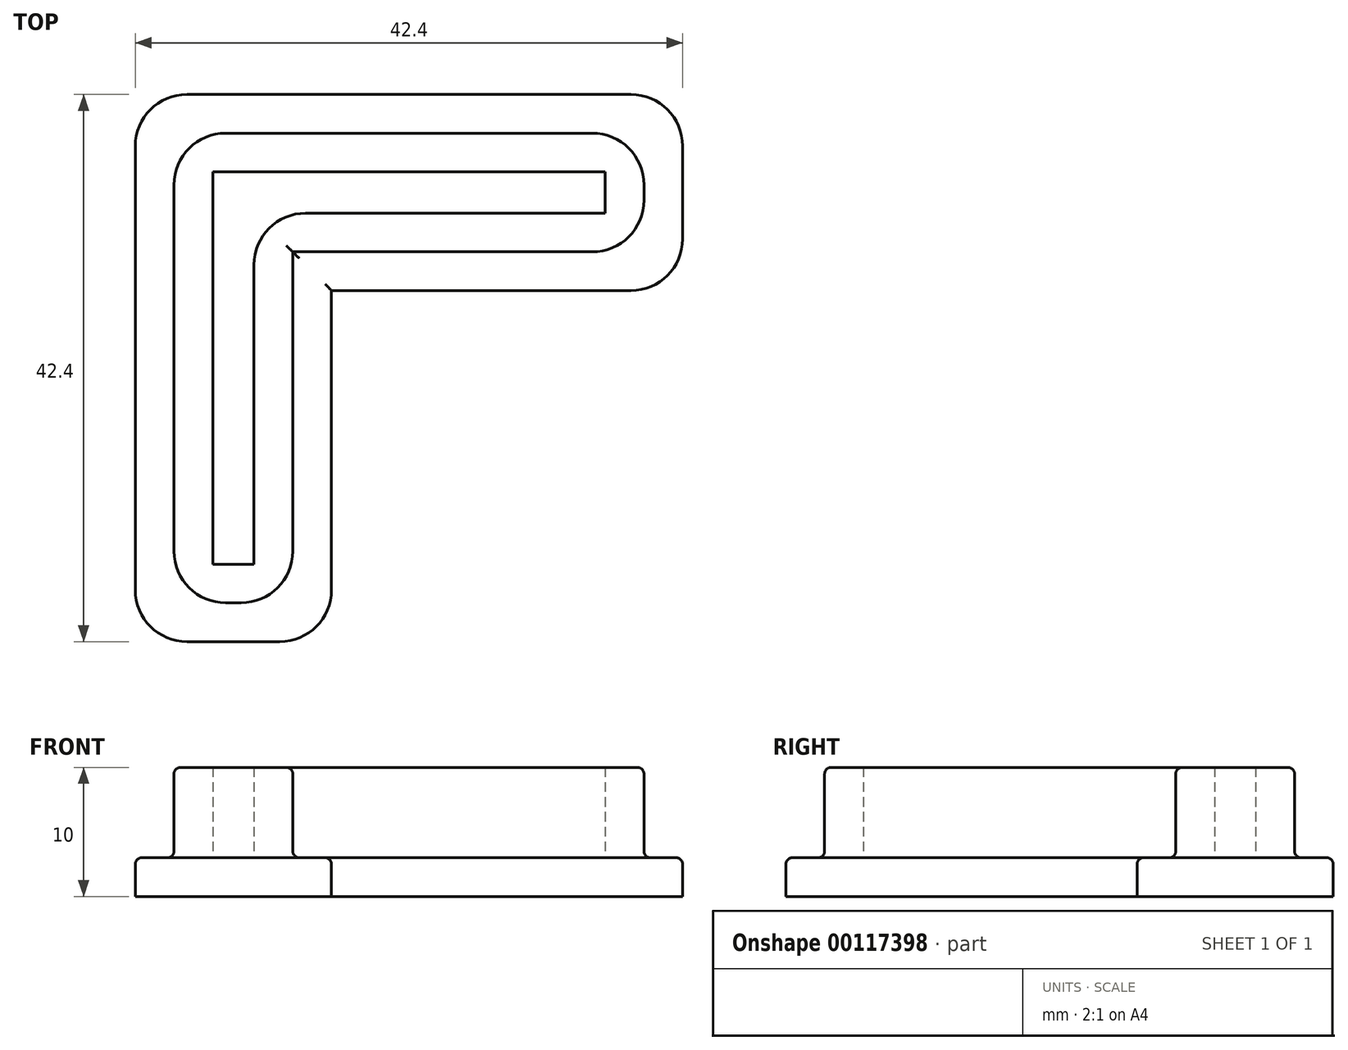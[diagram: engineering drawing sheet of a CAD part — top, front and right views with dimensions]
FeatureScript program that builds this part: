
annotation { "Feature Type Name" : "Feature", "Feature Type Description" : "" }
export const myFeature = defineFeature(function(context is Context, id is Id, definition is map)
    precondition{}
    {
        {
            var Q0;
            Q0=qCreatedBy(makeId("Top.planeOp"),FACE);
            var sketch = newSketch(context, id + "F0", { "sketchPlane" : qUnion([Q0])});
            skLineSegment(sketch, "E0", {"start": v(-4.93, -14.55) * mm, "end": v(-4.93, 15.85) * mm});
            skLineSegment(sketch, "E1", {"start": v(-4.93, 15.85) * mm, "end": v(25.47, 15.85) * mm});
            skLineSegment(sketch, "E2", {"start": v(25.47, 15.85) * mm, "end": v(25.47, 12.65) * mm});
            skLineSegment(sketch, "E3", {"start": v(25.47, 12.65) * mm, "end": v(-1.73, 12.65) * mm});
            skLineSegment(sketch, "E4", {"start": v(-1.73, 12.65) * mm, "end": v(-1.73, -14.55) * mm});
            skLineSegment(sketch, "E5", {"start": v(-1.73, -14.55) * mm, "end": v(-4.93, -14.55) * mm});
            skLineSegment(sketch, "E6.0", {"start": v(28.47, 9.65) * mm, "end": v(1.27, 9.65) * mm});
            skLineSegment(sketch, "E6.1", {"start": v(1.27, -17.55) * mm, "end": v(-7.93, -17.55) * mm});
            skLineSegment(sketch, "E6.2", {"start": v(-7.93, -17.55) * mm, "end": v(-7.93, 18.85) * mm});
            skLineSegment(sketch, "E6.3", {"start": v(1.27, 9.65) * mm, "end": v(1.27, -17.55) * mm});
            skLineSegment(sketch, "E6.4", {"start": v(-7.93, 18.85) * mm, "end": v(28.47, 18.85) * mm});
            skLineSegment(sketch, "E6.5", {"start": v(28.47, 18.85) * mm, "end": v(28.47, 9.65) * mm});
            skLineSegment(sketch, "E7.0", {"start": v(-10.93, -20.55) * mm, "end": v(-10.93, 21.85) * mm});
            skLineSegment(sketch, "E7.1", {"start": v(31.47, 21.85) * mm, "end": v(31.47, 6.65) * mm});
            skLineSegment(sketch, "E7.2", {"start": v(31.47, 6.65) * mm, "end": v(4.27, 6.65) * mm});
            skLineSegment(sketch, "E7.3", {"start": v(-10.93, 21.85) * mm, "end": v(31.47, 21.85) * mm});
            skLineSegment(sketch, "E7.4", {"start": v(4.27, 6.65) * mm, "end": v(4.27, -20.55) * mm});
            skLineSegment(sketch, "E7.5", {"start": v(4.27, -20.55) * mm, "end": v(-10.93, -20.55) * mm});
            skSolve(sketch);
        }
        {
            var Q0;
            Q0=makeQuery(id+"F0.imprint","IMPRINT",FACE,{"disambiguationData":[TD([[makeQuery(id+"F0.imprint","IMPRINT",EDGE,{"derivedFrom":sQuery(id+"F0.wireOp",EDGE,"E0")}),-1.0]])]});
            var Q1;
            Q1=makeQuery(id+"F0.imprint","IMPRINT",FACE,{"disambiguationData":[TD([[makeQuery(id+"F0.imprint","IMPRINT",EDGE,{"derivedFrom":sQuery(id+"F0.wireOp",EDGE,"E6.0")}),1.0]])]});
            var Q2;
            Q2=makeQuery(id+"F0.imprint","IMPRINT",FACE,{"disambiguationData":[TD([[makeQuery(id+"F0.imprint","IMPRINT",EDGE,{"derivedFrom":sQuery(id+"F0.wireOp",EDGE,"E0")}),1.0]])]});
            extrude(context, id + "F1", {"entities" : qUnion([Q0, Q1, Q2]), "depth" : 3 * mm});
        }
        {
            var Q0;
            Q0=makeQuery(id+"F0.imprint","IMPRINT",FACE,{"disambiguationData":[TD([[makeQuery(id+"F0.imprint","IMPRINT",EDGE,{"derivedFrom":sQuery(id+"F0.wireOp",EDGE,"E0")}),1.0]])]});
            extrude(context, id + "F2", {"entities" : qUnion([Q0]), "operationType" : NewBodyOperationType.ADD, "depth" : 10 * mm});
        }
        {
            var Q0;
            Q0=makeQuery(id+"F1.opExtrude","SWEPT_EDGE",EDGE,{"disambiguationData":[OSD([sQuery(id+"F0.wireOp",EDGE,"E7.4"),sQuery(id+"F0.wireOp",EDGE,"E7.5")])]});
            var Q1;
            Q1=makeQuery(id+"F1.opExtrude","SWEPT_EDGE",EDGE,{"disambiguationData":[OSD([sQuery(id+"F0.wireOp",EDGE,"E7.1"),sQuery(id+"F0.wireOp",EDGE,"E7.2")])]});
            var Q2;
            Q2=makeQuery(id+"F1.opExtrude","SWEPT_EDGE",EDGE,{"disambiguationData":[OSD([sQuery(id+"F0.wireOp",EDGE,"E7.1"),sQuery(id+"F0.wireOp",EDGE,"E7.3")])]});
            var Q3;
            Q3=makeQuery(id+"F1.opExtrude","SWEPT_EDGE",EDGE,{"disambiguationData":[OSD([sQuery(id+"F0.wireOp",EDGE,"E7.0"),sQuery(id+"F0.wireOp",EDGE,"E7.3")])]});
            var Q4;
            Q4=makeQuery(id+"F1.opExtrude","SWEPT_EDGE",EDGE,{"disambiguationData":[OSD([sQuery(id+"F0.wireOp",EDGE,"E7.0"),sQuery(id+"F0.wireOp",EDGE,"E7.5")])]});
            var Q5;
            Q5=makeQuery(id+"F2.opExtrude","SWEPT_EDGE",EDGE,{"disambiguationData":[OSD([sQuery(id+"F0.wireOp",EDGE,"E6.1"),sQuery(id+"F0.wireOp",EDGE,"E6.3")])]});
            var Q6;
            Q6=makeQuery(id+"F2.opExtrude","SWEPT_EDGE",EDGE,{"disambiguationData":[OSD([sQuery(id+"F0.wireOp",EDGE,"E6.0"),sQuery(id+"F0.wireOp",EDGE,"E6.5")])]});
            var Q7;
            Q7=makeQuery(id+"F2.opExtrude","SWEPT_EDGE",EDGE,{"disambiguationData":[OSD([sQuery(id+"F0.wireOp",EDGE,"E6.4"),sQuery(id+"F0.wireOp",EDGE,"E6.5")])]});
            var Q8;
            Q8=makeQuery(id+"F2.opExtrude","SWEPT_EDGE",EDGE,{"disambiguationData":[OSD([sQuery(id+"F0.wireOp",EDGE,"E6.1"),sQuery(id+"F0.wireOp",EDGE,"E6.2")])]});
            var Q9;
            Q9=makeQuery(id+"F2.opExtrude","SWEPT_EDGE",EDGE,{"disambiguationData":[OSD([sQuery(id+"F0.wireOp",EDGE,"E3"),sQuery(id+"F0.wireOp",EDGE,"E4")])]});
            var Q10;
            Q10=makeQuery(id+"F2.opExtrude","SWEPT_EDGE",EDGE,{"disambiguationData":[OSD([sQuery(id+"F0.wireOp",EDGE,"E6.2"),sQuery(id+"F0.wireOp",EDGE,"E6.4")])]});
            fillet(context, id + "F3", {"entities" : qUnion([Q0, Q1, Q2, Q3, Q4, Q5, Q6, Q7, Q8, Q9, Q10]), "radius" : 4 * mm, "tangentPropagation" : true, "allowEdgeOverflow" : false});
        }
        {
            var Q0;
            {var subQ0=sQuery(id+"F0.wireOp",EDGE,"E7.5");var subQ1=sQuery(id+"F0.wireOp",EDGE,"E7.4");var subQ2=sQuery(id+"F0.wireOp",EDGE,"E7.0");var subQ3=sQuery(id+"F0.wireOp",EDGE,"E7.1");var subQ4=sQuery(id+"F0.wireOp",EDGE,"E7.2");var subQ5=sQuery(id+"F0.wireOp",EDGE,"E7.3");Q0=makeQuery(id+"F2.boolean.opBoolean","SPLIT",FACE,{"disambiguationData":[TD([makeQuery(id+"F1.opExtrude","SWEPT_FACE",FACE,{"disambiguationData":[OSD([subQ2])]})])],"derivedFrom":makeQuery(id+"F1.opExtrude","CAP_FACE",FACE,{"disambiguationData":[OSD([subQ2,subQ3,subQ4,subQ5,subQ1,subQ0])],"isStart":false})});}
            var Q1;
            Q1=makeQuery(id+"F2.opExtrude","CAP_EDGE",EDGE,{"disambiguationData":[OSD([sQuery(id+"F0.wireOp",EDGE,"E6.2")])],"isStart":false});
            var Q2;
            {var subQ0=sQuery(id+"F0.wireOp",EDGE,"E6.4");var subQ1=sQuery(id+"F0.wireOp",EDGE,"E6.2");Q2=makeQuery(id+"F3.opFillet","BLEND_EDGE",EDGE,{"blendedFrom":[makeQuery(id+"F2.opExtrude","SWEPT_EDGE",EDGE,{"disambiguationData":[OSD([subQ1,subQ0])]}),makeQuery(id+"F2.opExtrude","CAP_FACE",FACE,{"disambiguationData":[OSD([sQuery(id+"F0.wireOp",EDGE,"E0"),sQuery(id+"F0.wireOp",EDGE,"E1"),sQuery(id+"F0.wireOp",EDGE,"E2"),sQuery(id+"F0.wireOp",EDGE,"E3"),sQuery(id+"F0.wireOp",EDGE,"E4"),sQuery(id+"F0.wireOp",EDGE,"E5"),sQuery(id+"F0.wireOp",EDGE,"E6.0"),sQuery(id+"F0.wireOp",EDGE,"E6.1"),subQ1,sQuery(id+"F0.wireOp",EDGE,"E6.3"),subQ0,sQuery(id+"F0.wireOp",EDGE,"E6.5")])],"isStart":false})],"blendedInto":[makeQuery(id+"F2.opExtrude","CAP_FACE",FACE,{"disambiguationData":[OSD([sQuery(id+"F0.wireOp",EDGE,"E0"),sQuery(id+"F0.wireOp",EDGE,"E1"),sQuery(id+"F0.wireOp",EDGE,"E2"),sQuery(id+"F0.wireOp",EDGE,"E3"),sQuery(id+"F0.wireOp",EDGE,"E4"),sQuery(id+"F0.wireOp",EDGE,"E5"),sQuery(id+"F0.wireOp",EDGE,"E6.0"),sQuery(id+"F0.wireOp",EDGE,"E6.1"),subQ1,sQuery(id+"F0.wireOp",EDGE,"E6.3"),subQ0,sQuery(id+"F0.wireOp",EDGE,"E6.5")])],"isStart":false})]});}
            var Q3;
            Q3=makeQuery(id+"F2.opExtrude","CAP_EDGE",EDGE,{"disambiguationData":[OSD([sQuery(id+"F0.wireOp",EDGE,"E6.4")])],"isStart":false});
            var Q4;
            {var subQ0=sQuery(id+"F0.wireOp",EDGE,"E6.5");var subQ1=sQuery(id+"F0.wireOp",EDGE,"E6.4");Q4=makeQuery(id+"F3.opFillet","BLEND_EDGE",EDGE,{"blendedFrom":[makeQuery(id+"F2.opExtrude","SWEPT_EDGE",EDGE,{"disambiguationData":[OSD([subQ1,subQ0])]}),makeQuery(id+"F2.opExtrude","CAP_FACE",FACE,{"disambiguationData":[OSD([sQuery(id+"F0.wireOp",EDGE,"E0"),sQuery(id+"F0.wireOp",EDGE,"E1"),sQuery(id+"F0.wireOp",EDGE,"E2"),sQuery(id+"F0.wireOp",EDGE,"E3"),sQuery(id+"F0.wireOp",EDGE,"E4"),sQuery(id+"F0.wireOp",EDGE,"E5"),sQuery(id+"F0.wireOp",EDGE,"E6.0"),sQuery(id+"F0.wireOp",EDGE,"E6.1"),sQuery(id+"F0.wireOp",EDGE,"E6.2"),sQuery(id+"F0.wireOp",EDGE,"E6.3"),subQ1,subQ0])],"isStart":false})],"blendedInto":[makeQuery(id+"F2.opExtrude","CAP_FACE",FACE,{"disambiguationData":[OSD([sQuery(id+"F0.wireOp",EDGE,"E0"),sQuery(id+"F0.wireOp",EDGE,"E1"),sQuery(id+"F0.wireOp",EDGE,"E2"),sQuery(id+"F0.wireOp",EDGE,"E3"),sQuery(id+"F0.wireOp",EDGE,"E4"),sQuery(id+"F0.wireOp",EDGE,"E5"),sQuery(id+"F0.wireOp",EDGE,"E6.0"),sQuery(id+"F0.wireOp",EDGE,"E6.1"),sQuery(id+"F0.wireOp",EDGE,"E6.2"),sQuery(id+"F0.wireOp",EDGE,"E6.3"),subQ1,subQ0])],"isStart":false})]});}
            fillet(context, id + "F4", {"entities" : qUnion([Q0, Q1, Q2, Q3, Q4]), "radius" : 0.5 * mm, "tangentPropagation" : true, "allowEdgeOverflow" : false});
        }
    });
